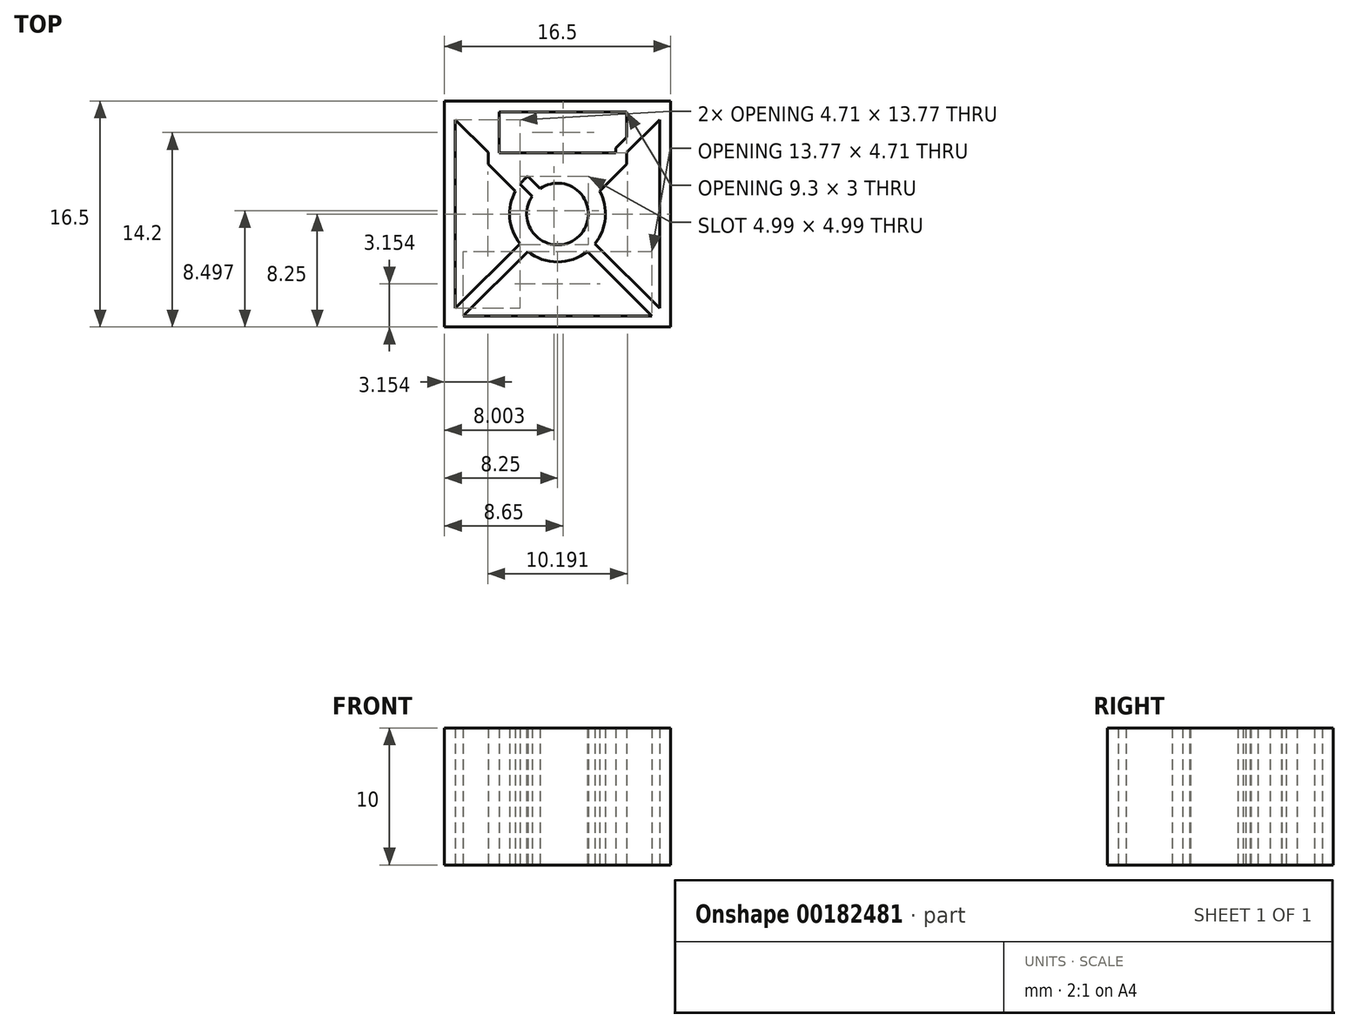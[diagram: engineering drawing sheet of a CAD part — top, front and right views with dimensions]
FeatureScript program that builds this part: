
annotation { "Feature Type Name" : "Feature", "Feature Type Description" : "" }
export const myFeature = defineFeature(function(context is Context, id is Id, definition is map)
    precondition{}
    {
        {
            var Q0;
            Q0=qCreatedBy(makeId("Top.planeOp"),FACE);
            var sketch = newSketch(context, id + "F0", { "sketchPlane" : qUnion([Q0])});
            skLineSegment(sketch, "E0.bottom", {"start": v(8.25, 8.25) * mm, "end": v(-8.25, 8.25) * mm});
            skLineSegment(sketch, "E0.top", {"start": v(8.25, -8.25) * mm, "end": v(-8.25, -8.25) * mm});
            skLineSegment(sketch, "E0.left", {"start": v(8.25, 8.25) * mm, "end": v(8.25, -8.25) * mm});
            skLineSegment(sketch, "E0.right", {"start": v(-8.25, 8.25) * mm, "end": v(-8.25, -8.25) * mm});
            skPoint(sketch, "E0.middle", {"position": v(0, 0) * mm});
            skLineSegment(sketch, "E1.0", {"start": v(7.45, 7.45) * mm, "end": v(-7.45, 7.45) * mm});
            skLineSegment(sketch, "E1.1", {"start": v(7.45, 7.45) * mm, "end": v(7.45, -7.45) * mm});
            skLineSegment(sketch, "E1.2", {"start": v(7.45, -7.45) * mm, "end": v(-7.45, -7.45) * mm});
            skLineSegment(sketch, "E1.3", {"start": v(-7.45, 7.45) * mm, "end": v(-7.45, -7.45) * mm});
            skLineSegment(sketch, "E2", {"start": v(-4.25, 7.45) * mm, "end": v(-4.25, 4.45) * mm});
            skLineSegment(sketch, "E3", {"start": v(-4.25, 4.45) * mm, "end": v(4.25, 4.45) * mm});
            skLineSegment(sketch, "E4", {"start": v(4.25, 4.45) * mm, "end": v(4.25, 7.45) * mm});
            skLineSegment(sketch, "E5", {"start": v(4.25, 7.45) * mm, "end": v(5.05, 7.45) * mm});
            skLineSegment(sketch, "E6", {"start": v(5.05, 7.45) * mm, "end": v(5.05, 3.65) * mm});
            skLineSegment(sketch, "E7", {"start": v(5.05, 3.65) * mm, "end": v(-5.05, 3.65) * mm});
            skLineSegment(sketch, "E8", {"start": v(-5.05, 3.65) * mm, "end": v(-5.05, 7.45) * mm});
            skLineSegment(sketch, "E9", {"start": v(0, 4.45) * mm, "end": v(0, 7.45) * mm, "construction": true});
            skCircle(sketch, "E10", {"center": v(0, 0) * mm, "radius": 2.25 * mm});
            skCircle(sketch, "E11", {"center": v(0, 0) * mm, "radius": 3.5 * mm});
            skLineSegment(sketch, "E12", {"start": v(-7.45, -7.45) * mm, "end": v(7.45, 7.45) * mm, "construction": true});
            skLineSegment(sketch, "E13", {"start": v(-7.45, 7.45) * mm, "end": v(7.45, -7.45) * mm, "construction": true});
            skLineSegment(sketch, "E14", {"start": v(-6.88, 7.45) * mm, "end": v(7.45, -6.88) * mm});
            skLineSegment(sketch, "E15", {"start": v(6.88, -7.45) * mm, "end": v(-7.45, 6.88) * mm});
            skLineSegment(sketch, "E16", {"start": v(6.88, 7.45) * mm, "end": v(-7.45, -6.88) * mm});
            skLineSegment(sketch, "E17", {"start": v(-6.88, -7.45) * mm, "end": v(7.45, 6.88) * mm});
            skLineSegment(sketch, "E18", {"start": v(-5.05, 3.65) * mm, "end": v(-3.07, 1.67) * mm});
            skLineSegment(sketch, "E19", {"start": v(5.05, 3.65) * mm, "end": v(3.07, 1.67) * mm});
            skSolve(sketch);
        }
        {
            var Q0;
            Q0=makeQuery(id+"F0.imprint","IMPRINT",FACE,{"disambiguationData":[TD([[makeQuery(id+"F0.imprint","IMPRINT",EDGE,{"derivedFrom":sQuery(id+"F0.wireOp",EDGE,"E0.bottom")}),1.0]])]});
            var Q1;
            {var subQ0=sQuery(id+"F0.wireOp",EDGE,"E2");Q1=makeQuery(id+"F0.imprint","IMPRINT",FACE,{"disambiguationData":[TD([[makeQuery(id+"F0.imprint","IMPRINT",EDGE,{"derivedFrom":subQ0}),-1.0]])]});}
            var Q2;
            {var subQ1=sQuery(id+"F0.wireOp",EDGE,"E1.0");var subQ5=sQuery(id+"F0.wireOp",EDGE,"E1.1");var subQ6=makeQuery(id+"F0.imprint","INTERSECT",VERTEX,{"derivedFrom":[subQ1,subQ5]});Q2=makeQuery(id+"F0.imprint","IMPRINT",FACE,{"disambiguationData":[TD([[makeQuery(id+"F0.imprint","IMPRINT",EDGE,{"disambiguationData":[TD([[subQ6,-1.0]])],"derivedFrom":subQ1}),1.0]])]});}
            var Q3;
            {var subQ1=sQuery(id+"F0.wireOp",EDGE,"E1.0");var subQ7=sQuery(id+"F0.wireOp",EDGE,"E1.3");var subQ8=makeQuery(id+"F0.imprint","INTERSECT",VERTEX,{"derivedFrom":[subQ1,subQ7]});Q3=makeQuery(id+"F0.imprint","IMPRINT",FACE,{"disambiguationData":[TD([[makeQuery(id+"F0.imprint","IMPRINT",EDGE,{"disambiguationData":[TD([[subQ8,1.0]])],"derivedFrom":subQ1}),1.0]])]});}
            var Q4;
            {var subQ0=sQuery(id+"F0.wireOp",EDGE,"E14");var subQ1=sQuery(id+"F0.wireOp",EDGE,"E10");var subQ2=makeQuery(id+"F0.imprint","INTERSECT",VERTEX,{"disambiguationData":[OD(0.0)],"derivedFrom":[subQ1,subQ0]});Q4=makeQuery(id+"F0.imprint","IMPRINT",FACE,{"disambiguationData":[TD([[makeQuery(id+"F0.imprint","IMPRINT",EDGE,{"disambiguationData":[TD([[subQ2,-1.0]])],"derivedFrom":subQ1}),-1.0]])]});}
            var Q5;
            {var subQ0=sQuery(id+"F0.wireOp",EDGE,"E15");var subQ1=sQuery(id+"F0.wireOp",EDGE,"E10");var subQ2=makeQuery(id+"F0.imprint","INTERSECT",VERTEX,{"disambiguationData":[OD(0.0)],"derivedFrom":[subQ1,subQ0]});Q5=makeQuery(id+"F0.imprint","IMPRINT",FACE,{"disambiguationData":[TD([[makeQuery(id+"F0.imprint","IMPRINT",EDGE,{"disambiguationData":[TD([[subQ2,-1.0]])],"derivedFrom":subQ1}),-1.0]])]});}
            var Q6;
            {var subQ0=sQuery(id+"F0.wireOp",EDGE,"E16");var subQ1=sQuery(id+"F0.wireOp",EDGE,"E10");var subQ2=makeQuery(id+"F0.imprint","INTERSECT",VERTEX,{"disambiguationData":[OD(1.0)],"derivedFrom":[subQ1,subQ0]});Q6=makeQuery(id+"F0.imprint","IMPRINT",FACE,{"disambiguationData":[TD([[makeQuery(id+"F0.imprint","IMPRINT",EDGE,{"disambiguationData":[TD([[subQ2,-1.0]])],"derivedFrom":subQ1}),-1.0]])]});}
            var Q7;
            {var subQ1=sQuery(id+"F0.wireOp",EDGE,"E1.3");var subQ7=sQuery(id+"F0.wireOp",EDGE,"E1.2");var subQ8=makeQuery(id+"F0.imprint","INTERSECT",VERTEX,{"derivedFrom":[subQ7,subQ1]});Q7=makeQuery(id+"F0.imprint","IMPRINT",FACE,{"disambiguationData":[TD([[makeQuery(id+"F0.imprint","IMPRINT",EDGE,{"disambiguationData":[TD([[subQ8,1.0]])],"derivedFrom":subQ7}),-1.0]])]});}
            var Q8;
            {var subQ0=sQuery(id+"F0.wireOp",EDGE,"E17");var subQ1=sQuery(id+"F0.wireOp",EDGE,"E10");var subQ2=makeQuery(id+"F0.imprint","INTERSECT",VERTEX,{"disambiguationData":[OD(1.0)],"derivedFrom":[subQ1,subQ0]});Q8=makeQuery(id+"F0.imprint","IMPRINT",FACE,{"disambiguationData":[TD([[makeQuery(id+"F0.imprint","IMPRINT",EDGE,{"disambiguationData":[TD([[subQ2,-1.0]])],"derivedFrom":subQ1}),-1.0]])]});}
            var Q9;
            {var subQ0=sQuery(id+"F0.wireOp",EDGE,"E15");var subQ1=sQuery(id+"F0.wireOp",EDGE,"E10");var subQ2=makeQuery(id+"F0.imprint","INTERSECT",VERTEX,{"disambiguationData":[OD(1.0)],"derivedFrom":[subQ1,subQ0]});Q9=makeQuery(id+"F0.imprint","IMPRINT",FACE,{"disambiguationData":[TD([[makeQuery(id+"F0.imprint","IMPRINT",EDGE,{"disambiguationData":[TD([[subQ2,-1.0]])],"derivedFrom":subQ1}),-1.0]])]});}
            var Q10;
            {var subQ0=sQuery(id+"F0.wireOp",EDGE,"E17");var subQ1=sQuery(id+"F0.wireOp",EDGE,"E10");var subQ2=makeQuery(id+"F0.imprint","INTERSECT",VERTEX,{"disambiguationData":[OD(0.0)],"derivedFrom":[subQ1,subQ0]});Q10=makeQuery(id+"F0.imprint","IMPRINT",FACE,{"disambiguationData":[TD([[makeQuery(id+"F0.imprint","IMPRINT",EDGE,{"disambiguationData":[TD([[subQ2,1.0]])],"derivedFrom":subQ1}),-1.0]])]});}
            var Q11;
            {var subQ1=sQuery(id+"F0.wireOp",EDGE,"E1.1");var subQ5=sQuery(id+"F0.wireOp",EDGE,"E1.2");var subQ6=makeQuery(id+"F0.imprint","INTERSECT",VERTEX,{"derivedFrom":[subQ1,subQ5]});Q11=makeQuery(id+"F0.imprint","IMPRINT",FACE,{"disambiguationData":[TD([[makeQuery(id+"F0.imprint","IMPRINT",EDGE,{"disambiguationData":[TD([[subQ6,1.0]])],"derivedFrom":subQ1}),-1.0]])]});}
            var Q12;
            {var subQ0=sQuery(id+"F0.wireOp",EDGE,"E16");var subQ1=sQuery(id+"F0.wireOp",EDGE,"E10");var subQ2=makeQuery(id+"F0.imprint","INTERSECT",VERTEX,{"disambiguationData":[OD(0.0)],"derivedFrom":[subQ1,subQ0]});Q12=makeQuery(id+"F0.imprint","IMPRINT",FACE,{"disambiguationData":[TD([[makeQuery(id+"F0.imprint","IMPRINT",EDGE,{"disambiguationData":[TD([[subQ2,1.0]])],"derivedFrom":subQ1}),-1.0]])]});}
            var Q13;
            {var subQ5=sQuery(id+"F0.wireOp",EDGE,"E4");var subQ6=sQuery(id+"F0.wireOp",EDGE,"E3");var subQ7=makeQuery(id+"F0.imprint","INTERSECT",VERTEX,{"derivedFrom":[subQ6,subQ5]});Q13=makeQuery(id+"F0.imprint","IMPRINT",FACE,{"disambiguationData":[TD([[makeQuery(id+"F0.imprint","IMPRINT",EDGE,{"disambiguationData":[TD([[subQ7,1.0]])],"derivedFrom":subQ6}),-1.0]])]});}
            var Q14;
            {var subQ0=sQuery(id+"F0.wireOp",EDGE,"E7");var subQ1=sQuery(id+"F0.wireOp",EDGE,"E6");var subQ2=makeQuery(id+"F0.imprint","INTERSECT",VERTEX,{"derivedFrom":[subQ1,subQ0]});Q14=makeQuery(id+"F0.imprint","IMPRINT",FACE,{"disambiguationData":[TD([[makeQuery(id+"F0.imprint","IMPRINT",EDGE,{"disambiguationData":[TD([[subQ2,1.0]])],"derivedFrom":subQ1}),-1.0]])]});}
            var Q15;
            {var subQ0=sQuery(id+"F0.wireOp",EDGE,"E5");Q15=makeQuery(id+"F0.imprint","IMPRINT",FACE,{"disambiguationData":[TD([[makeQuery(id+"F0.imprint","IMPRINT",EDGE,{"derivedFrom":subQ0}),-1.0]])]});}
            var Q16;
            {var subQ0=sQuery(id+"F0.wireOp",EDGE,"E14");var subQ1=sQuery(id+"F0.wireOp",EDGE,"E3");var subQ2=makeQuery(id+"F0.imprint","INTERSECT",VERTEX,{"derivedFrom":[subQ1,subQ0]});Q16=makeQuery(id+"F0.imprint","IMPRINT",FACE,{"disambiguationData":[TD([[makeQuery(id+"F0.imprint","IMPRINT",EDGE,{"disambiguationData":[TD([[subQ2,-1.0]])],"derivedFrom":subQ1}),-1.0]])]});}
            var Q17;
            {var subQ1=sQuery(id+"F0.wireOp",EDGE,"E1.0");var subQ3=sQuery(id+"F0.wireOp",EDGE,"E16");var subQ4=makeQuery(id+"F0.imprint","INTERSECT",VERTEX,{"derivedFrom":[subQ1,subQ3]});Q17=makeQuery(id+"F0.imprint","IMPRINT",FACE,{"disambiguationData":[TD([[makeQuery(id+"F0.imprint","IMPRINT",EDGE,{"disambiguationData":[TD([[subQ4,-1.0]])],"derivedFrom":subQ3}),-1.0]])]});}
            var Q18;
            {var subQ0=sQuery(id+"F0.wireOp",EDGE,"E8");var subQ1=sQuery(id+"F0.wireOp",EDGE,"E1.0");var subQ2=makeQuery(id+"F0.imprint","INTERSECT",VERTEX,{"derivedFrom":[subQ1,subQ0]});Q18=makeQuery(id+"F0.imprint","IMPRINT",FACE,{"disambiguationData":[TD([[makeQuery(id+"F0.imprint","IMPRINT",EDGE,{"disambiguationData":[TD([[subQ2,-1.0]])],"derivedFrom":subQ1}),1.0]])]});}
            var Q19;
            {var subQ8=sQuery(id+"F0.wireOp",EDGE,"E3");var subQ9=sQuery(id+"F0.wireOp",EDGE,"E2");var subQ10=makeQuery(id+"F0.imprint","INTERSECT",VERTEX,{"derivedFrom":[subQ9,subQ8]});Q19=makeQuery(id+"F0.imprint","IMPRINT",FACE,{"disambiguationData":[TD([[makeQuery(id+"F0.imprint","IMPRINT",EDGE,{"disambiguationData":[TD([[subQ10,1.0]])],"derivedFrom":subQ9}),-1.0]])]});}
            var Q20;
            {var subQ0=sQuery(id+"F0.wireOp",EDGE,"E8");var subQ1=sQuery(id+"F0.wireOp",EDGE,"E7");var subQ2=makeQuery(id+"F0.imprint","INTERSECT",VERTEX,{"derivedFrom":[subQ1,subQ0]});Q20=makeQuery(id+"F0.imprint","IMPRINT",FACE,{"disambiguationData":[TD([[makeQuery(id+"F0.imprint","IMPRINT",EDGE,{"disambiguationData":[TD([[subQ2,1.0]])],"derivedFrom":subQ1}),-1.0]])]});}
            var Q21;
            {var subQ0=sQuery(id+"F0.wireOp",EDGE,"E16");var subQ1=sQuery(id+"F0.wireOp",EDGE,"E7");var subQ2=makeQuery(id+"F0.imprint","INTERSECT",VERTEX,{"derivedFrom":[subQ1,subQ0]});Q21=makeQuery(id+"F0.imprint","IMPRINT",FACE,{"disambiguationData":[TD([[makeQuery(id+"F0.imprint","IMPRINT",EDGE,{"disambiguationData":[TD([[subQ2,-1.0]])],"derivedFrom":subQ1}),1.0]])]});}
            var Q22;
            {var subQ0=sQuery(id+"F0.wireOp",EDGE,"E14");var subQ1=sQuery(id+"F0.wireOp",EDGE,"E7");var subQ2=makeQuery(id+"F0.imprint","INTERSECT",VERTEX,{"derivedFrom":[subQ1,subQ0]});Q22=makeQuery(id+"F0.imprint","IMPRINT",FACE,{"disambiguationData":[TD([[makeQuery(id+"F0.imprint","IMPRINT",EDGE,{"disambiguationData":[TD([[subQ2,-1.0]])],"derivedFrom":subQ1}),1.0]])]});}
            var Q23;
            {var subQ0=sQuery(id+"F0.wireOp",EDGE,"E17");var subQ1=sQuery(id+"F0.wireOp",EDGE,"E7");var subQ2=makeQuery(id+"F0.imprint","INTERSECT",VERTEX,{"derivedFrom":[subQ1,subQ0]});Q23=makeQuery(id+"F0.imprint","IMPRINT",FACE,{"disambiguationData":[TD([[makeQuery(id+"F0.imprint","IMPRINT",EDGE,{"disambiguationData":[TD([[subQ2,-1.0]])],"derivedFrom":subQ1}),1.0]])]});}
            var Q24;
            {var subQ0=sQuery(id+"F0.wireOp",EDGE,"E11");var subQ1=sQuery(id+"F0.wireOp",EDGE,"E7");var subQ2=makeQuery(id+"F0.imprint","INTERSECT",VERTEX,{"disambiguationData":[OD(1.0)],"derivedFrom":[subQ1,subQ0]});Q24=makeQuery(id+"F0.imprint","IMPRINT",FACE,{"disambiguationData":[TD([[makeQuery(id+"F0.imprint","IMPRINT",EDGE,{"disambiguationData":[TD([[subQ2,-1.0]])],"derivedFrom":subQ1}),1.0]])]});}
            var Q25;
            {var subQ0=sQuery(id+"F0.wireOp",EDGE,"E11");var subQ1=sQuery(id+"F0.wireOp",EDGE,"E7");var subQ9=makeQuery(id+"F0.imprint","INTERSECT",VERTEX,{"disambiguationData":[OD(0.0)],"derivedFrom":[subQ1,subQ0]});Q25=makeQuery(id+"F0.imprint","IMPRINT",FACE,{"disambiguationData":[TD([[makeQuery(id+"F0.imprint","IMPRINT",EDGE,{"disambiguationData":[TD([[subQ9,-1.0]])],"derivedFrom":subQ1}),1.0]])]});}
            var Q26;
            {var subQ0=sQuery(id+"F0.wireOp",EDGE,"E11");var subQ1=sQuery(id+"F0.wireOp",EDGE,"E3");var subQ2=makeQuery(id+"F0.imprint","INTERSECT",VERTEX,{"disambiguationData":[OD(0.0)],"derivedFrom":[subQ1,subQ0]});Q26=makeQuery(id+"F0.imprint","IMPRINT",FACE,{"disambiguationData":[TD([[makeQuery(id+"F0.imprint","IMPRINT",EDGE,{"disambiguationData":[TD([[subQ2,-1.0]])],"derivedFrom":subQ1}),-1.0]])]});}
            var Q27;
            {var subQ0=sQuery(id+"F0.wireOp",EDGE,"E11");var subQ1=sQuery(id+"F0.wireOp",EDGE,"E3");var subQ2=makeQuery(id+"F0.imprint","INTERSECT",VERTEX,{"disambiguationData":[OD(1.0)],"derivedFrom":[subQ1,subQ0]});Q27=makeQuery(id+"F0.imprint","IMPRINT",FACE,{"disambiguationData":[TD([[makeQuery(id+"F0.imprint","IMPRINT",EDGE,{"disambiguationData":[TD([[subQ2,-1.0]])],"derivedFrom":subQ1}),-1.0]])]});}
            var Q28;
            {var subQ0=sQuery(id+"F0.wireOp",EDGE,"E18");Q28=makeQuery(id+"F0.imprint","IMPRINT",FACE,{"disambiguationData":[TD([[makeQuery(id+"F0.imprint","IMPRINT",EDGE,{"derivedFrom":subQ0}),1.0]])]});}
            var Q29;
            {var subQ0=sQuery(id+"F0.wireOp",EDGE,"E19");Q29=makeQuery(id+"F0.imprint","IMPRINT",FACE,{"disambiguationData":[TD([[makeQuery(id+"F0.imprint","IMPRINT",EDGE,{"derivedFrom":subQ0}),-1.0]])]});}
            var Q30;
            {var subQ0=sQuery(id+"F0.wireOp",EDGE,"E16");var subQ1=sQuery(id+"F0.wireOp",EDGE,"E10");var subQ2=makeQuery(id+"F0.imprint","INTERSECT",VERTEX,{"disambiguationData":[OD(0.0)],"derivedFrom":[subQ1,subQ0]});Q30=makeQuery(id+"F0.imprint","IMPRINT",FACE,{"disambiguationData":[TD([[makeQuery(id+"F0.imprint","IMPRINT",EDGE,{"disambiguationData":[TD([[subQ2,-1.0]])],"derivedFrom":subQ1}),-1.0]])]});}
            extrude(context, id + "F1", {"entities" : qUnion([Q0, Q1, Q2, Q3, Q4, Q5, Q6, Q7, Q8, Q9, Q10, Q11, Q12, Q13, Q14, Q15, Q16, Q17, Q18, Q19, Q20, Q21, Q22, Q23, Q24, Q25, Q26, Q27, Q28, Q29, Q30]), "depth" : 10 * mm});
        }
    });
